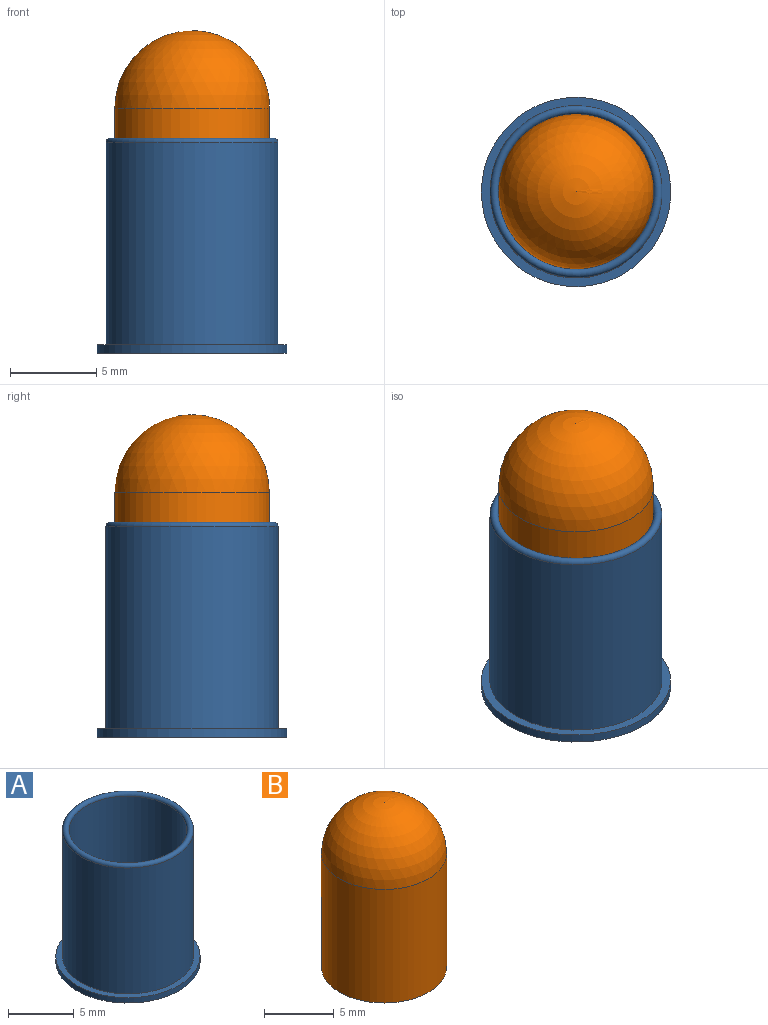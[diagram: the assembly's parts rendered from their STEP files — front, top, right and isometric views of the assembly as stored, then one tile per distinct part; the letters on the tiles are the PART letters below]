
ASSEMBLY  parts=2 mates=1
PART A: 293 faces, bbox 11.2x11.2x12.5 mm
  f0: plane 9x9mm, normal (0,0,1), area 63.6mm2, adj f5
  f1: plane 11x11mm, normal (0,0,-1), area 13.3mm2, adj f2,f291
  f2: cylinder r=5.5mm len=11mm, axis (0,0,-1), area 17.3mm2, adj f1,f3
  f3: plane 11x11mm, normal (0,0,1), area 16.5mm2, adj f2,f4
  f4: cylinder r=5mm len=11.75mm, axis (0,0,-1), area 369.1mm2, adj f3,f6
  f5: cylinder r=4.5mm len=11.75mm, axis (0,0,-1), area 332.2mm2, adj f0,f6
  f6: torus R=4.75mm, axis (0,0,-1), area 23.4mm2, adj f4,f5
  f7: plane 10x10mm, normal (0,0,-1), area 7.7mm2, adj f291,f292
  f8: plane 9.3x9.3mm, normal (0,0,-1), area 57.7mm2, adj f9,f10,f11,f12,f13,f14,f15,f16
  f9: plane 0.27x0.1mm, normal (1,0,0), area 0mm2, adj f8,f10,f36,f37
  f10: plane 0.1x0.06mm, normal (0,-1,0), area 0mm2, adj f8,f9,f11,f37
  f11: plane 0.27x0.1mm, normal (-1,0,0), area 0mm2, adj f8,f10,f12,f37
  f12: extruded ~0.11x0.1mm, area 0mm2, adj f8,f11,f13,f37
  f13: extruded ~0.1x0.1mm, area 0mm2, adj f8,f12,f14,f37
  f14: extruded ~0.1x0.08mm, area 0mm2, adj f8,f13,f15,f37
  f15: extruded ~0.1x0.05mm, area 0mm2, adj f8,f14,f16,f37
  f16: plane 0.1x0mm, normal (0,1,0), area 0mm2, adj f8,f15,f17,f37
  f17: extruded ~0.13x0.1mm, area 0mm2, adj f8,f16,f18,f37
  f18: extruded ~0.1x0.07mm, area 0mm2, adj f8,f17,f19,f37
  f19: extruded ~0.1x0.05mm, area 0mm2, adj f8,f18,f20,f37
  f20: plane 0.1x0mm, normal (0,1,0), area 0mm2, adj f8,f19,f21,f37
  f21: plane 0.1x0.06mm, normal (-0.98,0.18,0), area 0mm2, adj f8,f20,f22,f37
  f22: plane 0.1x0.05mm, normal (0,1,0), area 0mm2, adj f8,f21,f23,f37
  f23: plane 0.41x0.1mm, normal (1,0,0), area 0mm2, adj f8,f22,f24,f37
  f24: plane 0.1x0.06mm, normal (0,-1,0), area 0mm2, adj f8,f23,f25,f37
  f25: plane 0.21x0.1mm, normal (-1,0,0), area 0mm2, adj f8,f24,f26,f37
  f26: extruded ~0.11x0.1mm, area 0mm2, adj f8,f25,f27,f37
  f27: extruded ~0.1x0.09mm, area 0mm2, adj f8,f26,f28,f37
  f28: extruded ~0.1x0.07mm, area 0mm2, adj f8,f27,f29,f37
  f29: extruded ~0.1x0.07mm, area 0mm2, adj f8,f28,f30,f37
  f30: plane 0.27x0.1mm, normal (1,0,0), area 0mm2, adj f8,f29,f31,f37
  f31: plane 0.1x0.06mm, normal (0,-1,0), area 0mm2, adj f8,f30,f32,f37
  f32: plane 0.23x0.1mm, normal (-1,0,0), area 0mm2, adj f8,f31,f33,f37
  f33: extruded ~0.1x0.1mm, area 0mm2, adj f8,f32,f34,f37
  f34: extruded ~0.1x0.09mm, area 0mm2, adj f8,f33,f35,f37
  f35: extruded ~0.1x0.07mm, area 0mm2, adj f8,f34,f36,f37
  f36: extruded ~0.1x0.07mm, area 0mm2, adj f8,f9,f35,f37
  f37: plane 0.58x0.42mm, normal (0,0,-1), area 0.1mm2, adj f9,f10,f11,f12,f13,f14,f15,f16
  f38: plane 0.27x0.1mm, normal (-1,0,0), area 0mm2, adj f8,f39,f54,f55
  f39: plane 0.1x0.06mm, normal (0,1,0), area 0mm2, adj f8,f38,f40,f55
  f40: plane 0.27x0.1mm, normal (1,0,0), area 0mm2, adj f8,f39,f41,f55
  f41: extruded ~0.11x0.1mm, area 0mm2, adj f8,f40,f42,f55
  f42: extruded ~0.11x0.1mm, area 0mm2, adj f8,f41,f43,f55
  f43: extruded ~0.1x0.08mm, area 0mm2, adj f8,f42,f44,f55
  f44: extruded ~0.1x0.05mm, area 0mm2, adj f8,f43,f45,f55
  f45: plane 0.1x0mm, normal (0,-1,0), area 0mm2, adj f8,f44,f46,f55
  f46: plane 0.1x0.05mm, normal (0.99,-0.16,0), area 0mm2, adj f8,f45,f47,f55
  f47: plane 0.1x0.05mm, normal (0,-1,0), area 0mm2, adj f8,f46,f48,f55
  f48: plane 0.41x0.1mm, normal (-1,0,0), area 0mm2, adj f8,f47,f49,f55
  f49: plane 0.1x0.06mm, normal (0,1,0), area 0mm2, adj f8,f48,f50,f55
  f50: plane 0.21x0.1mm, normal (1,0,0), area 0mm2, adj f8,f49,f51,f55
  f51: extruded ~0.11x0.1mm, area 0mm2, adj f8,f50,f52,f55
  f52: extruded ~0.1x0.09mm, area 0mm2, adj f8,f51,f53,f55
  f53: extruded ~0.1x0.07mm, area 0mm2, adj f8,f52,f54,f55
  f54: extruded ~0.1x0.07mm, area 0mm2, adj f8,f38,f53,f55
  f55: plane 0.42x0.34mm, normal (0,0,-1), area 0.1mm2, adj f38,f39,f40,f41,f42,f43,f44,f45
  f56: plane 0.1x0.06mm, normal (0,-1,0), area 0mm2, adj f8,f57,f59,f60
  f57: plane 0.58x0.1mm, normal (-1,0,0), area 0.1mm2, adj f8,f56,f58,f60
  f58: plane 0.1x0.06mm, normal (0,1,0), area 0mm2, adj f8,f57,f59,f60
  f59: plane 0.58x0.1mm, normal (1,0,0), area 0.1mm2, adj f8,f56,f58,f60
  f60: plane 0.58x0.06mm, normal (0,0,-1), area 0mm2, adj f56,f57,f58,f59
  f61: plane 0.1x0.06mm, normal (0,-1,0), area 0mm2, adj f8,f62,f64,f65
  f62: plane 0.58x0.1mm, normal (-1,0,0), area 0.1mm2, adj f8,f61,f63,f65
  f63: plane 0.1x0.06mm, normal (0,1,0), area 0mm2, adj f8,f62,f64,f65
  f64: plane 0.58x0.1mm, normal (1,0,0), area 0.1mm2, adj f8,f61,f63,f65
  f65: plane 0.58x0.06mm, normal (0,0,-1), area 0mm2, adj f61,f62,f63,f64
  f66: extruded ~0.1x0.08mm, area 0mm2, adj f67,f84,f85,f284
  f67: extruded ~0.1x0.07mm, area 0mm2, adj f66,f68,f85,f284
  f68: extruded ~0.1x0.09mm, area 0mm2, adj f67,f69,f85,f284
  f69: plane 0.21x0.1mm, normal (0,1,0), area 0mm2, adj f68,f84,f85,f284
  f70: extruded ~0.14x0.1mm, area 0mm2, adj f8,f71,f83,f85
  f71: extruded ~0.1x0.07mm, area 0mm2, adj f8,f70,f72,f85
  f72: extruded ~0.1x0.06mm, area 0mm2, adj f8,f71,f73,f85
  f73: plane 0.1x0.06mm, normal (-1,0,0), area 0mm2, adj f8,f72,f74,f85
  f74: extruded ~0.13x0.1mm, area 0mm2, adj f8,f73,f75,f85
  f75: extruded ~0.1x0.1mm, area 0mm2, adj f8,f74,f76,f85
  f76: extruded ~0.11x0.1mm, area 0mm2, adj f8,f75,f77,f85
  f77: plane 0.28x0.1mm, normal (0,-1,0), area 0mm2, adj f8,f76,f78,f85
  f78: plane 0.1x0.04mm, normal (-1,0,0), area 0mm2, adj f8,f77,f79,f85
  f79: extruded ~0.13x0.1mm, area 0mm2, adj f8,f78,f80,f85
  f80: extruded ~0.12x0.1mm, area 0mm2, adj f8,f79,f81,f85
  f81: extruded ~0.13x0.1mm, area 0mm2, adj f8,f80,f82,f85
  f82: extruded ~0.16x0.1mm, area 0mm2, adj f8,f81,f83,f85
  f83: extruded ~0.15x0.1mm, area 0mm2, adj f8,f70,f82,f85
  f84: extruded ~0.1x0.09mm, area 0mm2, adj f66,f69,f85,f284
  f85: plane 0.42x0.35mm, normal (0,0,-1), area 0.1mm2, adj f66,f67,f68,f69,f70,f71,f72,f73
  f86: extruded ~0.1x0.09mm, area 0mm2, adj f87,f108,f109,f285
  f87: extruded ~0.1x0.09mm, area 0mm2, adj f86,f88,f109,f285
  f88: extruded ~0.12x0.1mm, area 0mm2, adj f87,f89,f109,f285
  f89: extruded ~0.12x0.1mm, area 0mm2, adj f88,f90,f109,f285
  f90: extruded ~0.1x0.09mm, area 0mm2, adj f89,f91,f109,f285
  f91: extruded ~0.1x0.09mm, area 0mm2, adj f90,f92,f109,f285
  f92: extruded ~0.12x0.1mm, area 0mm2, adj f91,f108,f109,f285
  f93: extruded ~0.13x0.1mm, area 0mm2, adj f8,f94,f107,f109
  f94: extruded ~0.13x0.1mm, area 0mm2, adj f8,f93,f95,f109
  f95: plane 0.1x0mm, normal (0,1,0), area 0mm2, adj f8,f94,f96,f109
  f96: extruded ~0.1x0.09mm, area 0mm2, adj f8,f95,f97,f109
  f97: plane 0.14x0.1mm, normal (-1,0,0), area 0mm2, adj f8,f96,f98,f109
  f98: plane 0.1x0.06mm, normal (0,1,0), area 0mm2, adj f8,f97,f99,f109
  f99: plane 0.58x0.1mm, normal (1,0,0), area 0.1mm2, adj f8,f98,f100,f109
  f100: plane 0.1x0.04mm, normal (0,-1,0), area 0mm2, adj f8,f99,f101,f109
  f101: plane 0.1x0.05mm, normal (-0.97,-0.24,0), area 0mm2, adj f8,f100,f102,f109
  f102: plane 0.1x0mm, normal (0,-1,0), area 0mm2, adj f8,f101,f103,f109
  f103: extruded ~0.1x0.06mm, area 0mm2, adj f8,f102,f104,f109
  f104: extruded ~0.1x0.07mm, area 0mm2, adj f8,f103,f105,f109
  f105: extruded ~0.12x0.1mm, area 0mm2, adj f8,f104,f106,f109
  f106: extruded ~0.16x0.1mm, area 0mm2, adj f8,f105,f107,f109
  f107: extruded ~0.16x0.1mm, area 0mm2, adj f8,f93,f106,f109
  f108: extruded ~0.12x0.1mm, area 0mm2, adj f86,f92,f109,f285
  f109: plane 0.59x0.36mm, normal (0,0,-1), area 0.1mm2, adj f86,f87,f88,f89,f90,f91,f92,f93
  f110: extruded ~0.1x0.09mm, area 0mm2, adj f111,f136,f137,f286
  f111: extruded ~0.1x0.06mm, area 0mm2, adj f110,f112,f137,f286
  f112: extruded ~0.1x0.05mm, area 0mm2, adj f111,f113,f137,f286
  f113: extruded ~0.1x0.06mm, area 0mm2, adj f112,f114,f137,f286
  f114: extruded ~0.11x0.1mm, area 0mm2, adj f113,f115,f137,f286
  f115: plane 0.1x0.06mm, normal (-0.04,-1,0), area 0mm2, adj f114,f116,f137,f286
  f116: plane 0.1x0.04mm, normal (1,0,0), area 0mm2, adj f115,f136,f137,f286
  f117: plane 0.1x0.06mm, normal (0.98,-0.21,0), area 0mm2, adj f8,f118,f135,f137
  f118: plane 0.1x0.05mm, normal (0,-1,0), area 0mm2, adj f8,f117,f119,f137
  f119: plane 0.28x0.1mm, normal (-1,0,0), area 0mm2, adj f8,f118,f120,f137
  f120: extruded ~0.1x0.1mm, area 0mm2, adj f8,f119,f121,f137
  f121: extruded ~0.11x0.1mm, area 0mm2, adj f8,f120,f122,f137
  f122: extruded ~0.1x0.07mm, area 0mm2, adj f8,f121,f123,f137
  f123: extruded ~0.1x0.07mm, area 0mm2, adj f8,f122,f124,f137
  f124: plane 0.1x0.05mm, normal (0.93,-0.37,0), area 0mm2, adj f8,f123,f125,f137
  f125: extruded ~0.12x0.1mm, area 0mm2, adj f8,f124,f126,f137
  f126: extruded ~0.1x0.07mm, area 0mm2, adj f8,f125,f127,f137
  f127: extruded ~0.1x0.07mm, area 0mm2, adj f8,f126,f128,f137
  f128: plane 0.1x0.03mm, normal (1,0,0), area 0mm2, adj f8,f127,f129,f137
  f129: plane 0.1x0.07mm, normal (0.03,1,0), area 0mm2, adj f8,f128,f130,f137
  f130: extruded ~0.2x0.13mm, area 0mm2, adj f8,f129,f131,f137
  f131: extruded ~0.1x0.09mm, area 0mm2, adj f8,f130,f132,f137
  f132: extruded ~0.1x0.1mm, area 0mm2, adj f8,f131,f133,f137
  f133: extruded ~0.1x0.08mm, area 0mm2, adj f8,f132,f134,f137
  f134: extruded ~0.1x0.06mm, area 0mm2, adj f8,f133,f135,f137
  f135: plane 0.1x0mm, normal (0,-1,0), area 0mm2, adj f8,f117,f134,f137
  f136: extruded ~0.1x0.09mm, area 0mm2, adj f110,f116,f137,f286
  f137: plane 0.42x0.33mm, normal (0,0,-1), area 0.1mm2, adj f110,f111,f112,f113,f114,f115,f116,f117
  f138: extruded ~0.1x0.05mm, area 0mm2, adj f8,f139,f150,f151
  f139: extruded ~0.1x0.07mm, area 0mm2, adj f8,f138,f140,f151
  f140: extruded ~0.1x0.06mm, area 0mm2, adj f8,f139,f141,f151
  f141: plane 0.1x0mm, normal (0,1,0), area 0mm2, adj f8,f140,f142,f151
  f142: plane 0.1x0.08mm, normal (-1,0.09,0), area 0mm2, adj f8,f141,f143,f151
  f143: plane 0.1x0.05mm, normal (0,1,0), area 0mm2, adj f8,f142,f144,f151
  f144: plane 0.41x0.1mm, normal (1,0,0), area 0mm2, adj f8,f143,f145,f151
  f145: plane 0.1x0.06mm, normal (0,-1,0), area 0mm2, adj f8,f144,f146,f151
  f146: plane 0.22x0.1mm, normal (-1,0,0), area 0mm2, adj f8,f145,f147,f151
  f147: extruded ~0.1x0.1mm, area 0mm2, adj f8,f146,f148,f151
  f148: extruded ~0.1x0.09mm, area 0mm2, adj f8,f147,f149,f151
  f149: extruded ~0.1x0.04mm, area 0mm2, adj f8,f148,f150,f151
  f150: plane 0.1x0.06mm, normal (-0.99,-0.15,0), area 0mm2, adj f8,f138,f149,f151
  f151: plane 0.42x0.24mm, normal (0,0,-1), area 0mm2, adj f138,f139,f140,f141,f142,f143,f144,f145
  f152: extruded ~0.1x0.09mm, area 0mm2, adj f153,f178,f179,f287
  f153: extruded ~0.1x0.06mm, area 0mm2, adj f152,f154,f179,f287
  f154: extruded ~0.1x0.05mm, area 0mm2, adj f153,f155,f179,f287
  f155: extruded ~0.1x0.06mm, area 0mm2, adj f154,f156,f179,f287
  f156: extruded ~0.11x0.1mm, area 0mm2, adj f155,f157,f179,f287
  f157: plane 0.1x0.06mm, normal (-0.04,-1,0), area 0mm2, adj f156,f158,f179,f287
  f158: plane 0.1x0.04mm, normal (1,0,0), area 0mm2, adj f157,f178,f179,f287
  f159: plane 0.1x0.06mm, normal (0.98,-0.21,0), area 0mm2, adj f8,f160,f177,f179
  f160: plane 0.1x0.05mm, normal (0,-1,0), area 0mm2, adj f8,f159,f161,f179
  f161: plane 0.28x0.1mm, normal (-1,0,0), area 0mm2, adj f8,f160,f162,f179
  f162: extruded ~0.1x0.1mm, area 0mm2, adj f8,f161,f163,f179
  f163: extruded ~0.11x0.1mm, area 0mm2, adj f8,f162,f164,f179
  f164: extruded ~0.1x0.07mm, area 0mm2, adj f8,f163,f165,f179
  f165: extruded ~0.1x0.07mm, area 0mm2, adj f8,f164,f166,f179
  f166: plane 0.1x0.05mm, normal (0.93,-0.37,0), area 0mm2, adj f8,f165,f167,f179
  f167: extruded ~0.12x0.1mm, area 0mm2, adj f8,f166,f168,f179
  f168: extruded ~0.1x0.07mm, area 0mm2, adj f8,f167,f169,f179
  f169: extruded ~0.1x0.07mm, area 0mm2, adj f8,f168,f170,f179
  f170: plane 0.1x0.03mm, normal (1,0,0), area 0mm2, adj f8,f169,f171,f179
  f171: plane 0.1x0.07mm, normal (0.03,1,0), area 0mm2, adj f8,f170,f172,f179
  f172: extruded ~0.2x0.13mm, area 0mm2, adj f8,f171,f173,f179
  f173: extruded ~0.1x0.09mm, area 0mm2, adj f8,f172,f174,f179
  f174: extruded ~0.1x0.1mm, area 0mm2, adj f8,f173,f175,f179
  f175: extruded ~0.1x0.08mm, area 0mm2, adj f8,f174,f176,f179
  f176: extruded ~0.1x0.06mm, area 0mm2, adj f8,f175,f177,f179
  f177: plane 0.1x0mm, normal (0,-1,0), area 0mm2, adj f8,f159,f176,f179
  f178: extruded ~0.1x0.09mm, area 0mm2, adj f152,f158,f179,f287
  f179: plane 0.42x0.33mm, normal (0,0,-1), area 0.1mm2, adj f152,f153,f154,f155,f156,f157,f158,f159
  f180: plane 0.1x0.06mm, normal (0,1,0), area 0mm2, adj f181,f194,f195,f288
  f181: plane 0.22x0.1mm, normal (-1,0,0), area 0mm2, adj f180,f182,f195,f288
  f182: plane 0.1x0.07mm, normal (0,-1,0), area 0mm2, adj f181,f183,f195,f288
  f183: extruded ~0.11x0.1mm, area 0mm2, adj f182,f184,f195,f288
  f184: extruded ~0.1x0.08mm, area 0mm2, adj f183,f185,f195,f288
  f185: extruded ~0.1x0.09mm, area 0mm2, adj f184,f194,f195,f288
  f186: extruded ~0.13x0.1mm, area 0mm2, adj f8,f187,f193,f195
  f187: extruded ~0.2x0.16mm, area 0mm2, adj f8,f186,f188,f195
  f188: plane 0.14x0.1mm, normal (0,1,0), area 0mm2, adj f8,f187,f189,f195
  f189: plane 0.55x0.1mm, normal (1,0,0), area 0.1mm2, adj f8,f188,f190,f195
  f190: plane 0.1x0.06mm, normal (0,-1,0), area 0mm2, adj f8,f189,f191,f195
  f191: plane 0.21x0.1mm, normal (-1,0,0), area 0mm2, adj f8,f190,f192,f195
  f192: plane 0.1x0.06mm, normal (0,-1,0), area 0mm2, adj f8,f191,f193,f195
  f193: extruded ~0.16x0.1mm, area 0mm2, adj f8,f186,f192,f195
  f194: extruded ~0.12x0.1mm, area 0mm2, adj f180,f185,f195,f288
  f195: plane 0.55x0.35mm, normal (0,0,-1), area 0.1mm2, adj f180,f181,f182,f183,f184,f185,f186,f187
  f196: cylinder r=1.6mm len=3.2mm, axis (0,0,-1), area 1mm2, adj f8,f197
  f197: plane 3.2x3.2mm, normal (0,0,-1), area 1mm2, adj f196,f290
  f198: plane 2.8x2.8mm, normal (0,0,-1), area 6.2mm2, adj f290
  f199: plane 0.56x0.1mm, normal (1,0,0), area 0.1mm2, adj f8,f200,f226,f227
  f200: plane 0.13x0.1mm, normal (0,-1,0), area 0mm2, adj f8,f199,f201,f227
  f201: plane 0.56x0.1mm, normal (-1,0,0), area 0.1mm2, adj f8,f200,f202,f227
  f202: extruded ~0.24x0.1mm, area 0mm2, adj f8,f201,f203,f227
  f203: extruded ~0.22x0.1mm, area 0mm2, adj f8,f202,f204,f227
  f204: extruded ~0.17x0.1mm, area 0mm2, adj f8,f203,f205,f227
  f205: extruded ~0.11x0.11mm, area 0mm2, adj f8,f204,f206,f227
  f206: plane 0.1x0.01mm, normal (0,1,0), area 0mm2, adj f8,f205,f207,f227
  f207: extruded ~0.27x0.15mm, area 0mm2, adj f8,f206,f208,f227
  f208: extruded ~0.15x0.1mm, area 0mm2, adj f8,f207,f209,f227
  f209: extruded ~0.1x0.1mm, area 0mm2, adj f8,f208,f210,f227
  f210: plane 0.1x0.01mm, normal (0,1,0), area 0mm2, adj f8,f209,f211,f227
  f211: plane 0.12x0.1mm, normal (-0.98,0.18,0), area 0mm2, adj f8,f210,f212,f227
  f212: plane 0.11x0.1mm, normal (0,1,0), area 0mm2, adj f8,f211,f213,f227
  f213: plane 0.86x0.1mm, normal (1,0,0), area 0.1mm2, adj f8,f212,f214,f227
  f214: plane 0.13x0.1mm, normal (0,-1,0), area 0mm2, adj f8,f213,f215,f227
  f215: plane 0.45x0.1mm, normal (-1,0,0), area 0mm2, adj f8,f214,f216,f227
  f216: extruded ~0.24x0.1mm, area 0mm2, adj f8,f215,f217,f227
  f217: extruded ~0.18x0.1mm, area 0mm2, adj f8,f216,f218,f227
  f218: extruded ~0.14x0.1mm, area 0mm2, adj f8,f217,f219,f227
  f219: extruded ~0.16x0.1mm, area 0mm2, adj f8,f218,f220,f227
  f220: plane 0.56x0.1mm, normal (1,0,0), area 0.1mm2, adj f8,f219,f221,f227
  f221: plane 0.13x0.1mm, normal (0,-1,0), area 0mm2, adj f8,f220,f222,f227
  f222: plane 0.48x0.1mm, normal (-1,0,0), area 0mm2, adj f8,f221,f223,f227
  f223: extruded ~0.22x0.1mm, area 0mm2, adj f8,f222,f224,f227
  f224: extruded ~0.18x0.1mm, area 0mm2, adj f8,f223,f225,f227
  f225: extruded ~0.14x0.1mm, area 0mm2, adj f8,f224,f226,f227
  f226: extruded ~0.16x0.1mm, area 0mm2, adj f8,f199,f225,f227
  f227: plane 1.23x0.88mm, normal (0,0,-1), area 0.4mm2, adj f199,f200,f201,f202,f203,f204,f205,f206
  f228: extruded ~0.17x0.1mm, area 0mm2, adj f229,f253,f254,f289
  f229: extruded ~0.13x0.1mm, area 0mm2, adj f228,f230,f254,f289
  f230: extruded ~0.11x0.1mm, area 0mm2, adj f229,f231,f254,f289
  f231: extruded ~0.15x0.1mm, area 0mm2, adj f230,f232,f254,f289
  f232: extruded ~0.11x0.1mm, area 0mm2, adj f231,f233,f254,f289
  f233: extruded ~0.1x0.1mm, area 0mm2, adj f232,f234,f254,f289
  f234: extruded ~0.13x0.1mm, area 0mm2, adj f233,f235,f254,f289
  f235: extruded ~0.17x0.1mm, area 0mm2, adj f234,f236,f254,f289
  f236: extruded ~0.18x0.1mm, area 0mm2, adj f235,f253,f254,f289
  f237: extruded ~0.68x0.52mm, area 0.1mm2, adj f8,f238,f252,f254
  f238: extruded ~0.27x0.1mm, area 0mm2, adj f8,f237,f239,f254
  f239: extruded ~0.18x0.14mm, area 0mm2, adj f8,f238,f240,f254
  f240: extruded ~0.21x0.1mm, area 0mm2, adj f8,f239,f241,f254
  f241: extruded ~0.26x0.1mm, area 0mm2, adj f8,f240,f242,f254
  f242: extruded ~0.28x0.1mm, area 0mm2, adj f8,f241,f243,f254
  f243: extruded ~0.26x0.1mm, area 0mm2, adj f8,f242,f244,f254
  f244: extruded ~0.24x0.1mm, area 0mm2, adj f8,f243,f245,f254
  f245: extruded ~0.16x0.1mm, area 0mm2, adj f8,f244,f246,f254
  f246: extruded ~0.12x0.1mm, area 0mm2, adj f8,f245,f247,f254
  f247: plane 0.1x0.01mm, normal (0,-1,0), area 0mm2, adj f8,f246,f248,f254
  f248: extruded ~0.36x0.11mm, area 0mm2, adj f8,f247,f249,f254
  f249: extruded ~0.29x0.12mm, area 0mm2, adj f8,f248,f250,f254
  f250: extruded ~0.14x0.1mm, area 0mm2, adj f8,f249,f251,f254
  f251: plane 0.11x0.1mm, normal (1,0,0), area 0mm2, adj f8,f250,f252,f254
  f252: extruded ~0.15x0.1mm, area 0mm2, adj f8,f237,f251,f254
  f253: extruded ~0.2x0.1mm, area 0mm2, adj f228,f236,f254,f289
  f254: plane 1.18x0.75mm, normal (0,0,-1), area 0.3mm2, adj f228,f229,f230,f231,f232,f233,f234,f235
  f255: plane 0.56x0.1mm, normal (1,0,0), area 0.1mm2, adj f8,f256,f282,f283
  f256: plane 0.13x0.1mm, normal (0,-1,0), area 0mm2, adj f8,f255,f257,f283
  f257: plane 0.56x0.1mm, normal (-1,0,0), area 0.1mm2, adj f8,f256,f258,f283
  f258: extruded ~0.24x0.1mm, area 0mm2, adj f8,f257,f259,f283
  f259: extruded ~0.22x0.1mm, area 0mm2, adj f8,f258,f260,f283
  f260: extruded ~0.17x0.1mm, area 0mm2, adj f8,f259,f261,f283
  f261: extruded ~0.11x0.11mm, area 0mm2, adj f8,f260,f262,f283
  f262: plane 0.1x0.01mm, normal (0,1,0), area 0mm2, adj f8,f261,f263,f283
  f263: extruded ~0.27x0.15mm, area 0mm2, adj f8,f262,f264,f283
  f264: extruded ~0.15x0.1mm, area 0mm2, adj f8,f263,f265,f283
  f265: extruded ~0.1x0.1mm, area 0mm2, adj f8,f264,f266,f283
  f266: plane 0.1x0.01mm, normal (0,1,0), area 0mm2, adj f8,f265,f267,f283
  f267: plane 0.12x0.1mm, normal (-0.98,0.18,0), area 0mm2, adj f8,f266,f268,f283
  f268: plane 0.11x0.1mm, normal (0,1,0), area 0mm2, adj f8,f267,f269,f283
  f269: plane 0.86x0.1mm, normal (1,0,0), area 0.1mm2, adj f8,f268,f270,f283
  f270: plane 0.13x0.1mm, normal (0,-1,0), area 0mm2, adj f8,f269,f271,f283
  f271: plane 0.45x0.1mm, normal (-1,0,0), area 0mm2, adj f8,f270,f272,f283
  f272: extruded ~0.24x0.1mm, area 0mm2, adj f8,f271,f273,f283
  f273: extruded ~0.18x0.1mm, area 0mm2, adj f8,f272,f274,f283
  f274: extruded ~0.14x0.1mm, area 0mm2, adj f8,f273,f275,f283
  f275: extruded ~0.16x0.1mm, area 0mm2, adj f8,f274,f276,f283
  f276: plane 0.56x0.1mm, normal (1,0,0), area 0.1mm2, adj f8,f275,f277,f283
  f277: plane 0.13x0.1mm, normal (0,-1,0), area 0mm2, adj f8,f276,f278,f283
  f278: plane 0.48x0.1mm, normal (-1,0,0), area 0mm2, adj f8,f277,f279,f283
  f279: extruded ~0.22x0.1mm, area 0mm2, adj f8,f278,f280,f283
  f280: extruded ~0.18x0.1mm, area 0mm2, adj f8,f279,f281,f283
  f281: extruded ~0.14x0.1mm, area 0mm2, adj f8,f280,f282,f283
  f282: extruded ~0.16x0.1mm, area 0mm2, adj f8,f255,f281,f283
  f283: plane 1.23x0.88mm, normal (0,0,-1), area 0.4mm2, adj f255,f256,f257,f258,f259,f260,f261,f262
  f284: plane 0.21x0.12mm, normal (0,0,-1), area 0mm2, adj f66,f67,f68,f69,f84
  f285: plane 0.32x0.23mm, normal (0,0,-1), area 0.1mm2, adj f86,f87,f88,f89,f90,f91,f92,f108
  f286: plane 0.2x0.16mm, normal (0,0,-1), area 0mm2, adj f110,f111,f112,f113,f114,f115,f116,f136
  f287: plane 0.2x0.16mm, normal (0,0,-1), area 0mm2, adj f152,f153,f154,f155,f156,f157,f158,f178
  f288: plane 0.22x0.22mm, normal (0,0,-1), area 0mm2, adj f180,f181,f182,f183,f184,f185,f194
  f289: plane 0.52x0.49mm, normal (0,0,-1), area 0.2mm2, adj f228,f229,f230,f231,f232,f233,f234,f235
  f290: torus R=1.4mm, axis (0,0,1), area 1.4mm2, adj f197,f198
  f291: torus R=5.1mm, axis (0,0,1), area 5mm2, adj f1,f7
  f292: torus R=4.65mm, axis (0,0,1), area 4.7mm2, adj f7,f8
PART B: 3 faces, bbox 9x9x14.5 mm
  f0: plane 9x9mm, normal (0,0,-1), area 63.6mm2, adj f1
  f1: cylinder r=4.5mm len=10mm, axis (0,0,1), area 282.7mm2, adj f0,f2
  f2: sphere r=4.5mm, area 127.2mm2, adj f1
PLACE A t=(4.14,1.43,-1.43)mm
PLACE B t=(4.14,1.43,2.32)mm
MATE fastened B.f1 <-> A.f2  axis (0,0,1) through (4.14,1.43,7.32)mm
